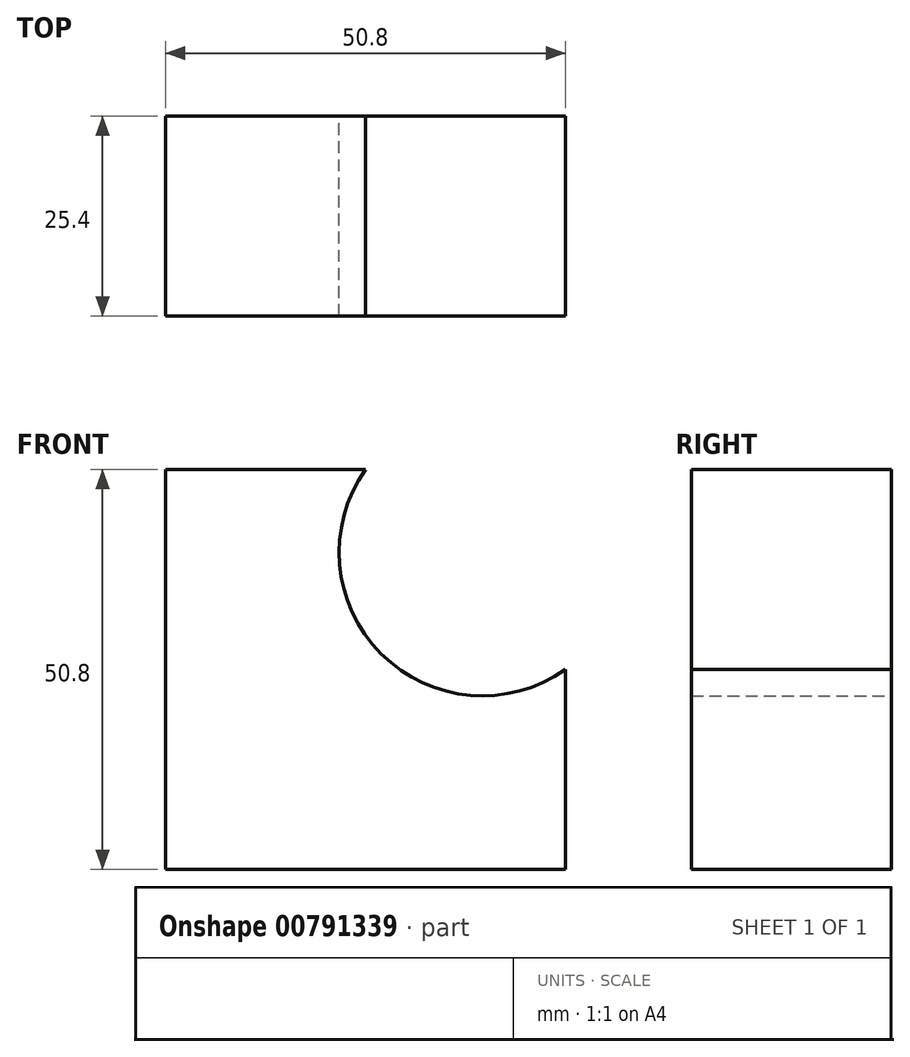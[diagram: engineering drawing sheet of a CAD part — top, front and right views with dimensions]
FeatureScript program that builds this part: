
annotation { "Feature Type Name" : "Feature", "Feature Type Description" : "" }
export const myFeature = defineFeature(function(context is Context, id is Id, definition is map)
    precondition{}
    {
        {
            var Q0;
            Q0=qCreatedBy(makeId("Front.planeOp"),FACE);
            var sketch = newSketch(context, id + "F0", { "sketchPlane" : qUnion([Q0])});
            skLineSegment(sketch, "E0", {"start": v(0, 50.8) * mm, "end": v(0, 0) * mm});
            skLineSegment(sketch, "E1", {"start": v(0, 0) * mm, "end": v(50.8, 0) * mm});
            skLineSegment(sketch, "E2", {"start": v(50.8, 0) * mm, "end": v(50.8, 25.4) * mm});
            skLineSegment(sketch, "E3", {"start": v(0, 50.8) * mm, "end": v(25.4, 50.8) * mm});
            skArc(sketch, "E4", {"start": v(25.4, 50.8) * mm, "mid": v(27.4, 27.4) * mm, "end": v(50.8, 25.4) * mm});
            skSolve(sketch);
        }
        {
            var Q0;
            Q0=qSketchRegion(id+"F0",true);
            extrude(context, id + "F1", {"entities" : qUnion([Q0]), "depth" : 25.4 * mm, "offsetDistance" : 25.4 * mm});
        }
    });
